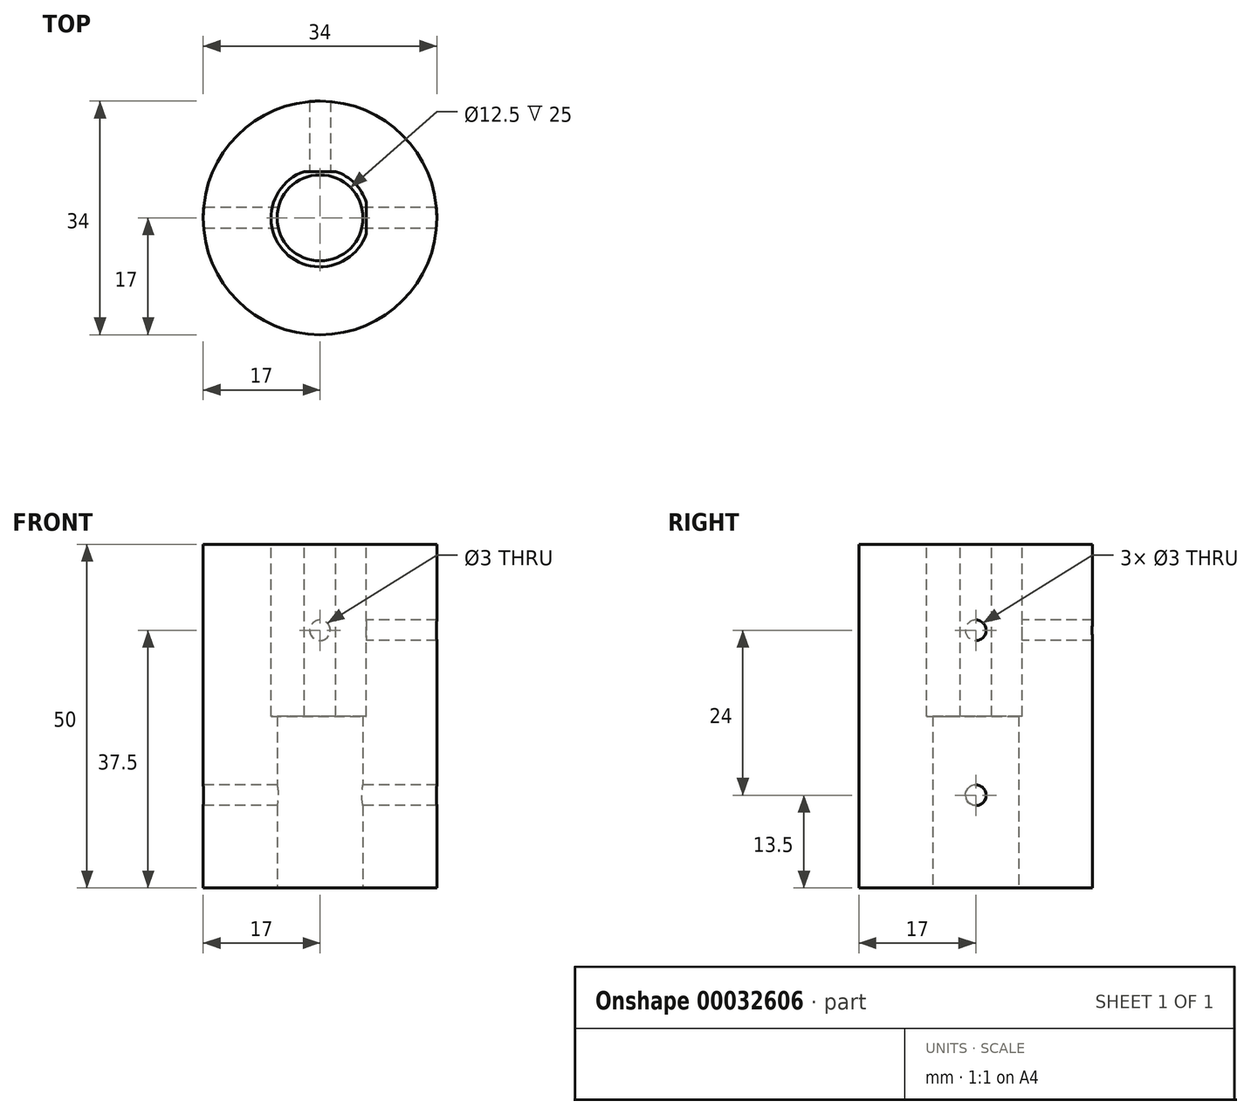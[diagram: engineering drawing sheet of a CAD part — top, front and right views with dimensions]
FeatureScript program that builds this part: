
annotation { "Feature Type Name" : "Feature", "Feature Type Description" : "" }
export const myFeature = defineFeature(function(context is Context, id is Id, definition is map)
    precondition{}
    {
        {
            var Q0;
            Q0=qCreatedBy(makeId("Top.planeOp"),FACE);
            var sketch = newSketch(context, id + "F0", { "sketchPlane" : qUnion([Q0])});
            skCircle(sketch, "E0", {"center": v(0, 0) * mm, "radius": 17 * mm});
            skCircle(sketch, "E1", {"center": v(0, 0) * mm, "radius": 6.25 * mm});
            skSolve(sketch);
        }
        {
            var Q0;
            Q0=makeQuery(id+"F0.imprint","IMPRINT",FACE,{"disambiguationData":[TD([[makeQuery(id+"F0.imprint","IMPRINT",EDGE,{"derivedFrom":sQuery(id+"F0.wireOp",EDGE,"E0")}),1.0]])]});
            var Q1;
            Q1=makeQuery(id+"F0.imprint","IMPRINT",FACE,{"disambiguationData":[TD([[makeQuery(id+"F0.imprint","IMPRINT",EDGE,{"derivedFrom":sQuery(id+"F0.wireOp",EDGE,"E1")}),1.0]])]});
            extrude(context, id + "F1", {"entities" : qUnion([Q0, Q1]), "depth" : 50 * mm});
        }
        {
            var Q0;
            Q0=makeQuery(id+"F1.opExtrude","CAP_FACE",FACE,{"disambiguationData":[OSD([sQuery(id+"F0.wireOp",EDGE,"E0"),sQuery(id+"F0.wireOp",EDGE,"E1")])],"isStart":false});
            var sketch = newSketch(context, id + "F2", { "sketchPlane" : qUnion([Q0])});
            skCircle(sketch, "E2", {"center": v(0, 0) * mm, "radius": 7.12 * mm});
            skLineSegment(sketch, "E3", {"start": v(0, 0) * mm, "end": v(0, 6.75) * mm, "construction": true});
            skLineSegment(sketch, "E4", {"start": v(0, 0) * mm, "end": v(6.75, 0) * mm, "construction": true});
            skLineSegment(sketch, "E5.bottom", {"start": v(6.75, 6.75) * mm, "end": v(-6.75, 6.75) * mm});
            skLineSegment(sketch, "E5.top", {"start": v(6.75, -6.75) * mm, "end": v(-6.75, -6.75) * mm});
            skLineSegment(sketch, "E5.left", {"start": v(6.75, 6.75) * mm, "end": v(6.75, -6.75) * mm});
            skLineSegment(sketch, "E5.right", {"start": v(-6.75, 6.75) * mm, "end": v(-6.75, -6.75) * mm});
            skSolve(sketch);
        }
        {
            var Q0;
            Q0=makeQuery(id+"F0.imprint","IMPRINT",FACE,{"disambiguationData":[TD([[makeQuery(id+"F0.imprint","IMPRINT",EDGE,{"derivedFrom":sQuery(id+"F0.wireOp",EDGE,"E1")}),1.0]])]});
            extrude(context, id + "F3", {"entities" : qUnion([Q0]), "operationType" : NewBodyOperationType.REMOVE, "depth" : 25 * mm});
        }
        {
            var Q0;
            {var subQ1=sQuery(id+"F2.wireOp",EDGE,"E2");var subQ9=sQuery(id+"F2.wireOp",EDGE,"E5.bottom");var subQ11=makeQuery(id+"F2.imprint","INTERSECT",VERTEX,{"disambiguationData":[OD(0.0)],"derivedFrom":[subQ1,subQ9]});Q0=makeQuery(id+"F2.imprint","IMPRINT",FACE,{"disambiguationData":[TD([[makeQuery(id+"F2.imprint","IMPRINT",EDGE,{"disambiguationData":[TD([[subQ11,1.0]])],"derivedFrom":subQ1}),1.0]])]});}
            var Q1;
            {var subQ0=sQuery(id+"F2.wireOp",EDGE,"E5.right");var subQ1=sQuery(id+"F2.wireOp",EDGE,"E2");var subQ2=makeQuery(id+"F2.imprint","INTERSECT",VERTEX,{"disambiguationData":[OD(0.0)],"derivedFrom":[subQ1,subQ0]});Q1=makeQuery(id+"F2.imprint","IMPRINT",FACE,{"disambiguationData":[TD([[makeQuery(id+"F2.imprint","IMPRINT",EDGE,{"disambiguationData":[TD([[subQ2,-1.0]])],"derivedFrom":subQ1}),1.0]])]});}
            var Q2;
            {var subQ0=sQuery(id+"F2.wireOp",EDGE,"E5.top");var subQ1=sQuery(id+"F2.wireOp",EDGE,"E2");var subQ2=makeQuery(id+"F2.imprint","INTERSECT",VERTEX,{"disambiguationData":[OD(0.0)],"derivedFrom":[subQ1,subQ0]});Q2=makeQuery(id+"F2.imprint","IMPRINT",FACE,{"disambiguationData":[TD([[makeQuery(id+"F2.imprint","IMPRINT",EDGE,{"disambiguationData":[TD([[subQ2,-1.0]])],"derivedFrom":subQ1}),1.0]])]});}
            extrude(context, id + "F4", {"entities" : qUnion([Q0, Q1, Q2]), "operationType" : NewBodyOperationType.REMOVE, "oppositeDirection" : true, "depth" : 25 * mm});
        }
        {
            var Q0;
            Q0=makeQuery(id+"F4.boolean.opBoolean","COPY",FACE,{"derivedFrom":makeQuery(id+"F4.opExtrude","SWEPT_FACE",FACE,{"disambiguationData":[OSD([sQuery(id+"F2.wireOp",EDGE,"E5.left")])]})});
            var sketch = newSketch(context, id + "F5", { "sketchPlane" : qUnion([Q0])});
            skCircle(sketch, "E6", {"center": v(0, 37.5) * mm, "radius": 1.5 * mm});
            skPoint(sketch, "E6.centerSnap0", {"position": v(0, 50) * mm});
            skPoint(sketch, "E6.centerSnap1", {"position": v(-2.28, 37.5) * mm});
            skSolve(sketch);
        }
        {
            var Q0;
            Q0=makeQuery(id+"F5.imprint","IMPRINT",FACE,{"disambiguationData":[TD([[makeQuery(id+"F5.imprint","IMPRINT",EDGE,{"derivedFrom":sQuery(id+"F5.wireOp",EDGE,"E6")}),1.0]])]});
            extrude(context, id + "F6", {"entities" : qUnion([Q0]), "operationType" : NewBodyOperationType.REMOVE, "oppositeDirection" : true, "depth" : 25 * mm});
        }
        {
            var Q0;
            Q0=makeQuery(id+"F4.boolean.opBoolean","COPY",FACE,{"derivedFrom":makeQuery(id+"F4.opExtrude","SWEPT_FACE",FACE,{"disambiguationData":[OSD([sQuery(id+"F2.wireOp",EDGE,"E5.bottom")])]})});
            var sketch = newSketch(context, id + "F7", { "sketchPlane" : qUnion([Q0])});
            skCircle(sketch, "E7", {"center": v(0, 37.5) * mm, "radius": 1.5 * mm});
            skPoint(sketch, "E7.centerSnap0", {"position": v(0, 25) * mm});
            skPoint(sketch, "E7.centerSnap1", {"position": v(2.28, 37.5) * mm});
            skSolve(sketch);
        }
        {
            var Q0;
            Q0=makeQuery(id+"F7.imprint","IMPRINT",FACE,{"disambiguationData":[TD([[makeQuery(id+"F7.imprint","IMPRINT",EDGE,{"derivedFrom":sQuery(id+"F7.wireOp",EDGE,"E7")}),1.0]])]});
            extrude(context, id + "F8", {"entities" : qUnion([Q0]), "operationType" : NewBodyOperationType.REMOVE, "oppositeDirection" : true, "depth" : 25 * mm});
        }
        {
            var Q0;
            Q0=qCreatedBy(makeId("Right.planeOp"),FACE);
            var sketch = newSketch(context, id + "F9", { "sketchPlane" : qUnion([Q0])});
            skLineSegment(sketch, "E8", {"start": v(0, 0) * mm, "end": v(0, 13.5) * mm, "construction": true});
            skCircle(sketch, "E9", {"center": v(0, 13.5) * mm, "radius": 1.5 * mm});
            skSolve(sketch);
        }
        {
            var Q0;
            Q0 = qSketchRegion(id + "F9", true);
            extrude(context, id + "F10", {"entities" : qUnion([Q0]), "operationType" : NewBodyOperationType.REMOVE, "depth" : 100 * mm, "symmetric" : true});
        }
    });
